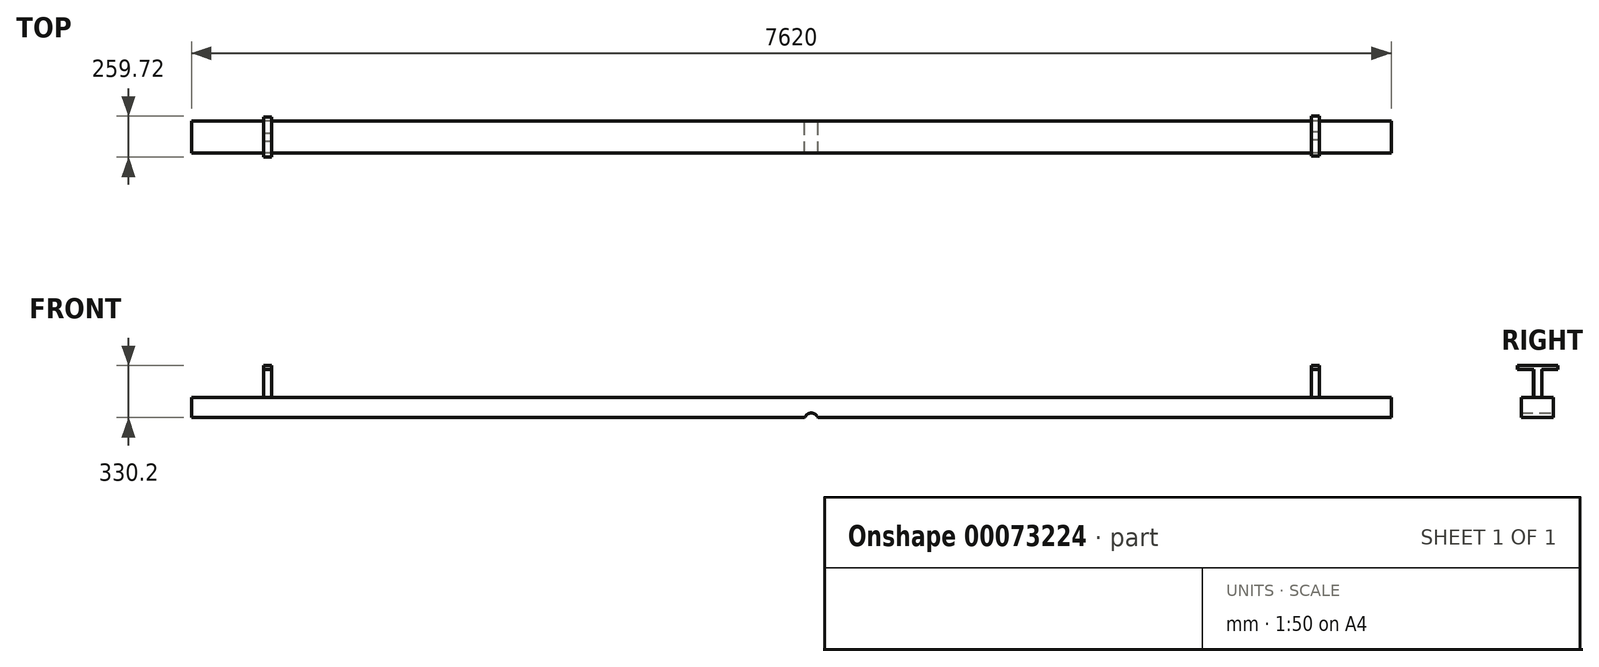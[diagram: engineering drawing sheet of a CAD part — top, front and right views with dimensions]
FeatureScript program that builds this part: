
annotation { "Feature Type Name" : "Feature", "Feature Type Description" : "" }
export const myFeature = defineFeature(function(context is Context, id is Id, definition is map)
    precondition{}
    {
        {
            var Q0;
            Q0=qCreatedBy(makeId("Front.planeOp"),FACE);
            var sketch = newSketch(context, id + "F0", { "sketchPlane" : qUnion([Q0])});
            skLineSegment(sketch, "E0.rect.bottom", {"start": v(3810, 63.5) * mm, "end": v(-3810, 63.5) * mm});
            skLineSegment(sketch, "E0.rect.top", {"start": v(3810, -63.5) * mm, "end": v(493.68, -63.5) * mm});
            skLineSegment(sketch, "E0.rect.left", {"start": v(3810, 63.5) * mm, "end": v(3810, -63.5) * mm});
            skLineSegment(sketch, "E0.rect.right", {"start": v(-3810, 63.5) * mm, "end": v(-3810, -63.5) * mm});
            skPoint(sketch, "E0.rect.middle", {"position": v(0, 0) * mm});
            skLineSegment(sketch, "E1", {"start": v(127, -220.94) * mm, "end": v(127, -63.5) * mm});
            skLineSegment(sketch, "E2.trimOffspring", {"start": v(420.72, -63.5) * mm, "end": v(168.76, -63.5) * mm});
            skPoint(sketch, "E3.start.orphan", {"position": v(127, -63.5) * mm});
            skLineSegment(sketch, "E4", {"start": v(493.68, -63.5) * mm, "end": v(420.72, -63.5) * mm});
            skLineSegment(sketch, "E5", {"start": v(127, -63.5) * mm, "end": v(127, -78.72) * mm});
            skArc(sketch, "E6", {"start": v(168.76, -63.5) * mm, "mid": v(127, -34.27) * mm, "end": v(85.24, -63.5) * mm});
            skLineSegment(sketch, "E7.trimOffspring", {"start": v(85.24, -63.5) * mm, "end": v(-3810, -63.5) * mm});
            skPoint(sketch, "E8.trimOffspring.end.orphan", {"position": v(127, 63.5) * mm});
            skSolve(sketch);
        }
        {
            var Q0;
            Q0 = qSketchRegion(id + "F0", true);
            extrude(context, id + "F1", {"entities" : qUnion([Q0]), "depth" : 203.2 * mm});
        }
        {
            var Q0;
            Q0=makeQuery(id+"F1.opExtrude","SWEPT_FACE",FACE,{"disambiguationData":[OSD([sQuery(id+"F0.wireOp",EDGE,"E0.rect.bottom")])]});
            var sketch = newSketch(context, id + "F2", { "sketchPlane" : qUnion([Q0])});
            skPoint(sketch, "E9.orphan", {"position": v(3810, -101.6) * mm});
            skLineSegment(sketch, "E10.rect.bottom", {"start": v(3352.8, -70.48) * mm, "end": v(3302, -70.48) * mm});
            skLineSegment(sketch, "E10.rect.top", {"start": v(3352.8, -121.28) * mm, "end": v(3302, -121.28) * mm});
            skLineSegment(sketch, "E10.rect.left", {"start": v(3352.8, -70.48) * mm, "end": v(3352.8, -121.28) * mm});
            skLineSegment(sketch, "E10.rect.right", {"start": v(3302, -70.48) * mm, "end": v(3302, -121.28) * mm});
            skPoint(sketch, "E10.rect.middle", {"position": v(3327.4, -95.88) * mm});
            skLineSegment(sketch, "E11", {"start": v(-3352.8, -127) * mm, "end": v(-3302, -127) * mm});
            skLineSegment(sketch, "E12.bottom", {"start": v(-3352.8, -76.2) * mm, "end": v(-3302, -76.2) * mm});
            skLineSegment(sketch, "E12.right", {"start": v(-3302, -76.2) * mm, "end": v(-3302, -127) * mm});
            skPoint(sketch, "E13.start.orphan", {"position": v(-3810, -101.6) * mm});
            skPoint(sketch, "E14.start.orphan", {"position": v(-3352.8, -101.6) * mm});
            skLineSegment(sketch, "E15.left", {"start": v(-3352.8, -76.2) * mm, "end": v(-3352.8, -127) * mm});
            skSolve(sketch);
        }
        {
            var Q0;
            Q0 = qSketchRegion(id + "F2", true);
            extrude(context, id + "F3", {"entities" : qUnion([Q0]), "operationType" : NewBodyOperationType.ADD, "depth" : 203.2 * mm});
        }
        {
            var Q0;
            Q0=makeQuery(id+"F3.opExtrude","SWEPT_FACE",FACE,{"disambiguationData":[OSD([sQuery(id+"F2.wireOp",EDGE,"E10.rect.top")])]});
            var sketch = newSketch(context, id + "F4", { "sketchPlane" : qUnion([Q0])});
            skLineSegment(sketch, "E16.bottom", {"start": v(3352.8, 266.7) * mm, "end": v(3302, 266.7) * mm});
            skLineSegment(sketch, "E17.bottom", {"start": v(3302, 266.7) * mm, "end": v(3352.8, 266.7) * mm});
            skLineSegment(sketch, "E17.top", {"start": v(3302, 241.3) * mm, "end": v(3352.8, 241.3) * mm});
            skLineSegment(sketch, "E17.left", {"start": v(3302, 266.7) * mm, "end": v(3302, 241.3) * mm});
            skLineSegment(sketch, "E17.right", {"start": v(3352.8, 266.7) * mm, "end": v(3352.8, 241.3) * mm});
            skSolve(sketch);
        }
        {
            var Q0;
            Q0 = qSketchRegion(id + "F4", true);
            extrude(context, id + "F5", {"entities" : qUnion([Q0]), "operationType" : NewBodyOperationType.ADD, "depth" : 101.6 * mm});
        }
        {
            var Q0;
            Q0=makeQuery(id+"F3.opExtrude","SWEPT_FACE",FACE,{"disambiguationData":[OSD([sQuery(id+"F2.wireOp",EDGE,"E10.rect.bottom")])]});
            var sketch = newSketch(context, id + "F6", { "sketchPlane" : qUnion([Q0])});
            skLineSegment(sketch, "E18.bottom", {"start": v(-3352.8, 266.7) * mm, "end": v(-3302, 266.7) * mm});
            skLineSegment(sketch, "E18.top", {"start": v(-3352.8, 241.3) * mm, "end": v(-3302, 241.3) * mm});
            skLineSegment(sketch, "E18.left", {"start": v(-3352.8, 266.7) * mm, "end": v(-3352.8, 241.3) * mm});
            skLineSegment(sketch, "E18.right", {"start": v(-3302, 266.7) * mm, "end": v(-3302, 241.3) * mm});
            skSolve(sketch);
        }
        {
            var Q0;
            Q0 = qSketchRegion(id + "F6", true);
            extrude(context, id + "F7", {"entities" : qUnion([Q0]), "operationType" : NewBodyOperationType.ADD, "depth" : 101.6 * mm});
        }
        {
            var Q0;
            Q0=makeQuery(id+"F3.opExtrude","SWEPT_FACE",FACE,{"disambiguationData":[OSD([sQuery(id+"F2.wireOp",EDGE,"E11")])]});
            var sketch = newSketch(context, id + "F8", { "sketchPlane" : qUnion([Q0])});
            skLineSegment(sketch, "E19.bottom", {"start": v(-3302, 266.7) * mm, "end": v(-3352.8, 266.7) * mm});
            skLineSegment(sketch, "E19.top", {"start": v(-3302, 241.3) * mm, "end": v(-3352.8, 241.3) * mm});
            skLineSegment(sketch, "E19.left", {"start": v(-3302, 266.7) * mm, "end": v(-3302, 241.3) * mm});
            skLineSegment(sketch, "E19.right", {"start": v(-3352.8, 266.7) * mm, "end": v(-3352.8, 241.3) * mm});
            skSolve(sketch);
        }
        {
            var Q0;
            Q0 = qSketchRegion(id + "F8", true);
            extrude(context, id + "F9", {"entities" : qUnion([Q0]), "operationType" : NewBodyOperationType.ADD, "depth" : 101.6 * mm});
        }
        {
            var Q0;
            Q0=makeQuery(id+"F3.opExtrude","SWEPT_FACE",FACE,{"disambiguationData":[OSD([sQuery(id+"F2.wireOp",EDGE,"E12.bottom")])]});
            var sketch = newSketch(context, id + "F10", { "sketchPlane" : qUnion([Q0])});
            skLineSegment(sketch, "E20.bottom", {"start": v(3302, 266.7) * mm, "end": v(3352.8, 266.7) * mm});
            skLineSegment(sketch, "E20.top", {"start": v(3302, 241.3) * mm, "end": v(3352.8, 241.3) * mm});
            skLineSegment(sketch, "E20.left", {"start": v(3302, 266.7) * mm, "end": v(3302, 241.3) * mm});
            skLineSegment(sketch, "E20.right", {"start": v(3352.8, 266.7) * mm, "end": v(3352.8, 241.3) * mm});
            skSolve(sketch);
        }
        {
            var Q0;
            Q0 = qSketchRegion(id + "F10", true);
            extrude(context, id + "F11", {"entities" : qUnion([Q0]), "operationType" : NewBodyOperationType.ADD, "depth" : 101.6 * mm});
        }
    });
